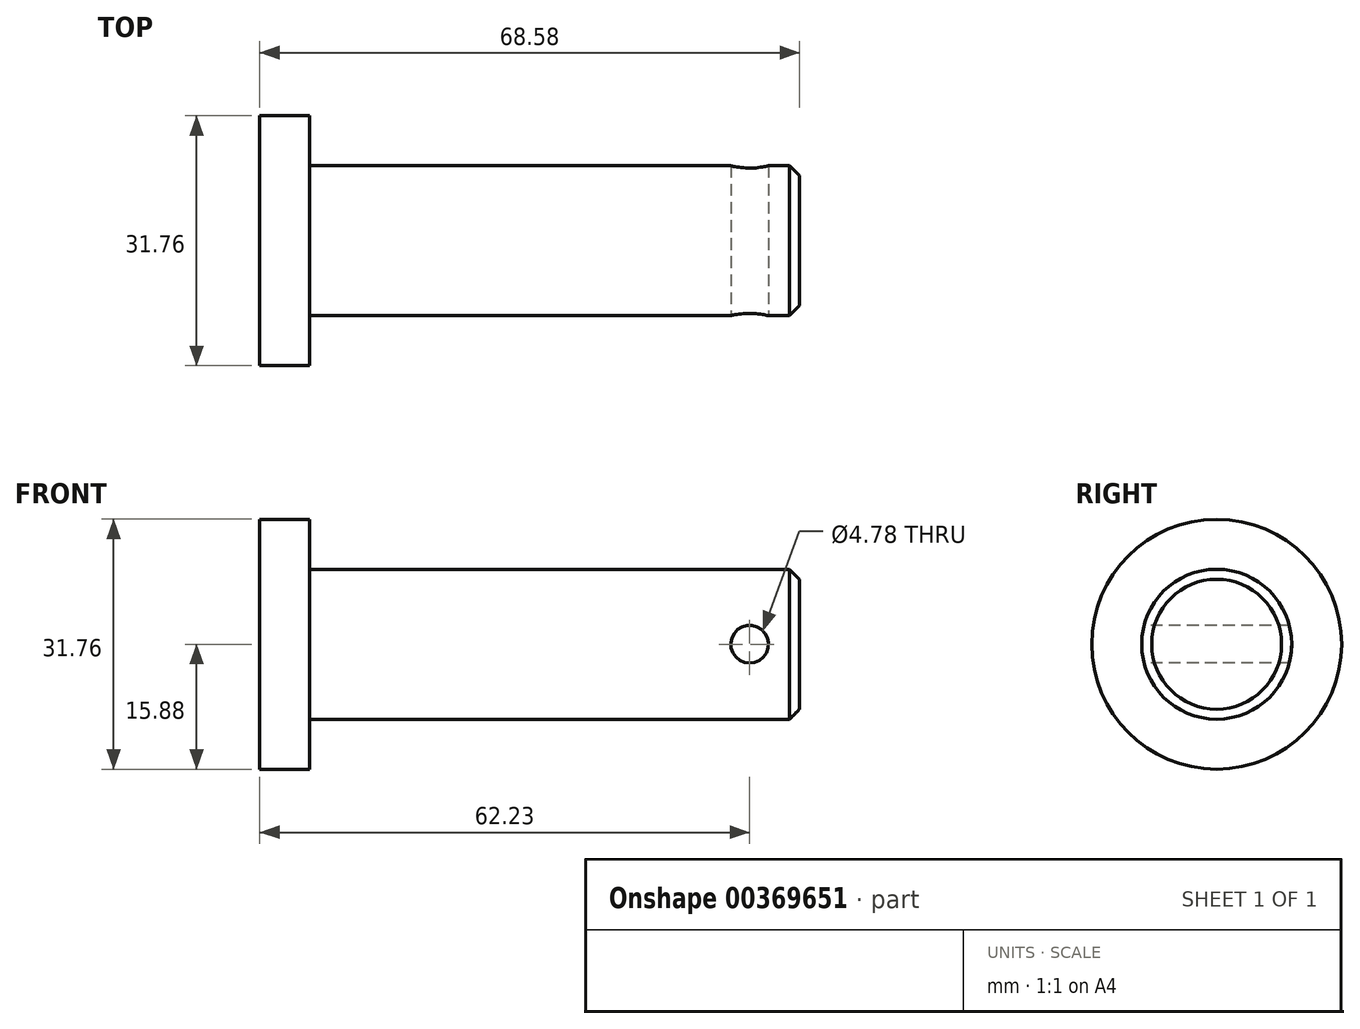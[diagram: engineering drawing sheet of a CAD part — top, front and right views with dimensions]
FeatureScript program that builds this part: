
annotation { "Feature Type Name" : "Feature", "Feature Type Description" : "" }
export const myFeature = defineFeature(function(context is Context, id is Id, definition is map)
    precondition{}
    {
        {
            var Q0;
            Q0=qCreatedBy(makeId("Right.planeOp"),FACE);
            var sketch = newSketch(context, id + "F0", { "sketchPlane" : qUnion([Q0])});
            skCircle(sketch, "E0", {"center": v(0, 0) * mm, "radius": 15.88 * mm});
            skSolve(sketch);
        }
        {
            var Q0;
            Q0 = qSketchRegion(id + "F0", true);
            extrude(context, id + "F1", {"entities" : qUnion([Q0]), "depth" : 6.35 * mm});
        }
        {
            var Q0;
            Q0=makeQuery(id+"F1.opExtrude","CAP_FACE",FACE,{"disambiguationData":[OSD([sQuery(id+"F0.wireOp",EDGE,"E0")])],"isStart":false});
            var sketch = newSketch(context, id + "F2", { "sketchPlane" : qUnion([Q0])});
            skCircle(sketch, "E1", {"center": v(0, 0) * mm, "radius": 9.53 * mm});
            skSolve(sketch);
        }
        {
            var Q0;
            Q0 = qSketchRegion(id + "F2", true);
            extrude(context, id + "F3", {"entities" : qUnion([Q0]), "operationType" : NewBodyOperationType.ADD, "depth" : 62.23 * mm});
        }
        {
            var Q0;
            Q0=qCreatedBy(makeId("Front.planeOp"),FACE);
            var sketch = newSketch(context, id + "F4", { "sketchPlane" : qUnion([Q0])});
            skCircle(sketch, "E2", {"center": v(62.23, 0) * mm, "radius": 2.39 * mm});
            skSolve(sketch);
        }
        {
            var Q0;
            Q0 = qSketchRegion(id + "F4", true);
            extrude(context, id + "F5", {"entities" : qUnion([Q0]), "operationType" : NewBodyOperationType.REMOVE, "endBound" : BoundingType.SYMMETRIC, "oppositeDirection" : true, "depth" : 25.4 * mm});
        }
        {
            var Q0;
            Q0=makeQuery(id+"F3.opExtrude","CAP_EDGE",EDGE,{"disambiguationData":[OSD([sQuery(id+"F2.wireOp",EDGE,"E1")])],"isStart":false});
            chamfer(context, id + "F6", {"entities" : qUnion([Q0]), "width" : 1.27 * mm, "tangentPropagation" : true});
        }
    });
